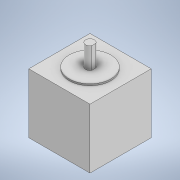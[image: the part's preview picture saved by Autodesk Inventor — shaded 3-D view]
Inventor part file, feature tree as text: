
AUTODESK INVENTOR PART (.ipt)
format: ipt  version: 2022 (Build 260153000, 153)  size: 111,616 bytes
history: native  units: mm
features: extrude x3, sketch x3
ambient origin geometry x8: Origin, YZ Plane, XZ Plane, XY Plane, X Axis, Y Axis, Z Axis, Center Point
bodies: Solid1 (feature_tree)
feature tree (6):
  extrude  "Extrusion1"  Depth=56.0mm
  extrude  "Extrusion2"  Depth=54.6mm
  extrude  "Extrusion3"  Depth=19.5mm
  sketch  "Sketch1"  dims[d0=56.0mm d1=56.0mm]
  sketch  "Sketch2"  dims[d2=54.6mm d3=0.0mm d4=38.0mm]
  sketch  "Sketch3"  dims[d5=1.5mm d6=0.0mm d7=8.0mm d8=0.5mm d9=19.5mm d10=0.0mm]
